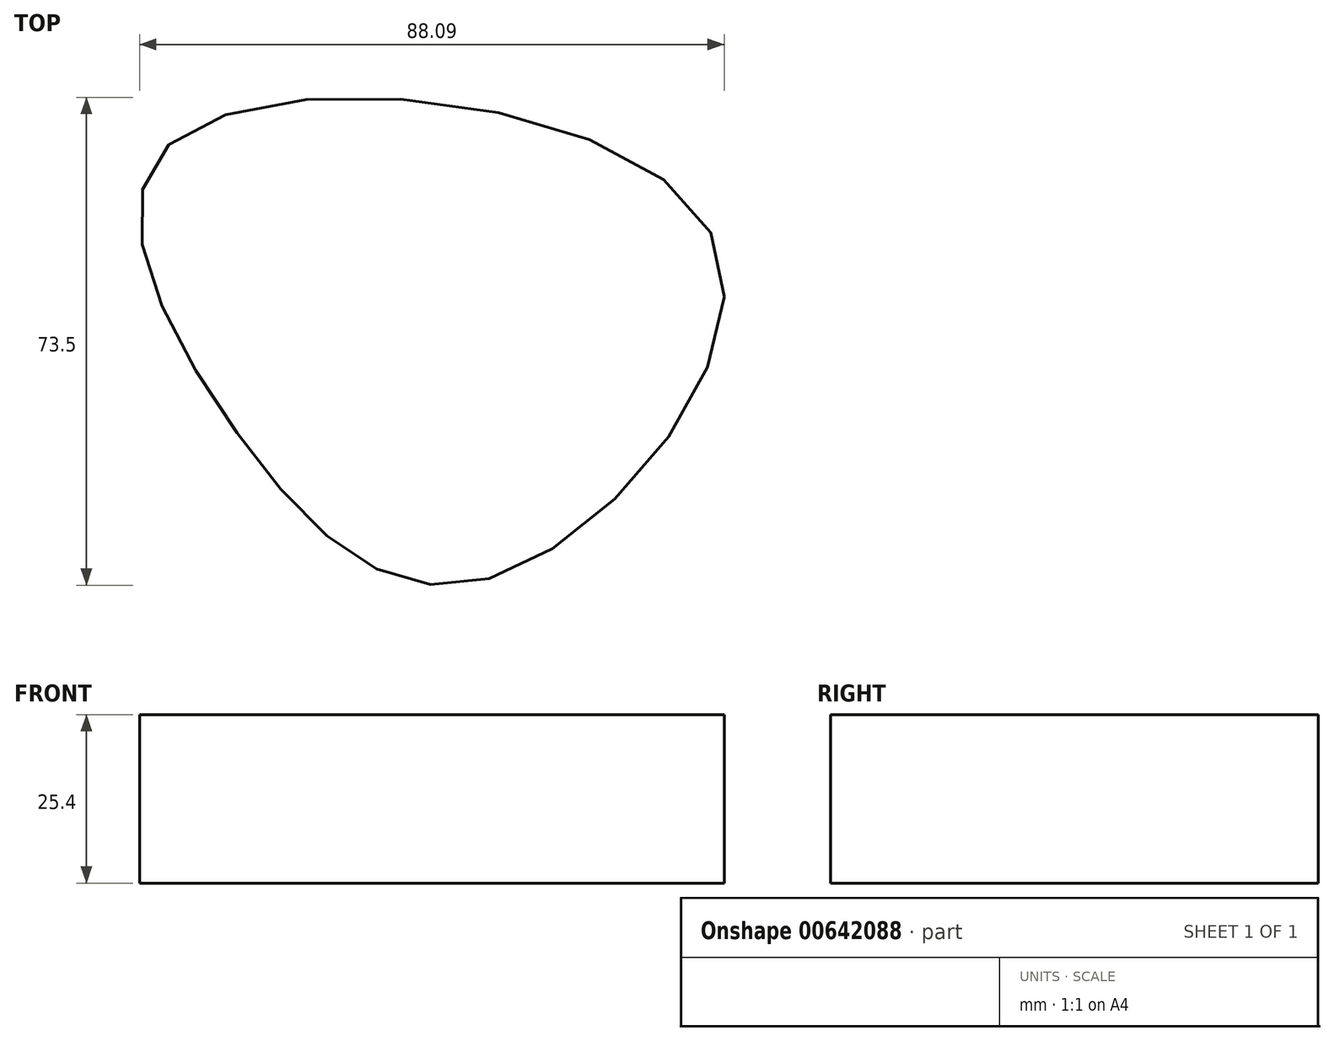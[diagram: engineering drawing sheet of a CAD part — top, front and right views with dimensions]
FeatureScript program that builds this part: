
annotation { "Feature Type Name" : "Feature", "Feature Type Description" : "" }
export const myFeature = defineFeature(function(context is Context, id is Id, definition is map)
    precondition{}
    {
        {
            var Q0;
            Q0=qCreatedBy(makeId("Top.planeOp"),FACE);
            var sketch = newSketch(context, id + "F0", { "sketchPlane" : qUnion([Q0])});
            skFitSpline(sketch, "E0", {"points": [v(-38.43, -12.93) * mm, v(-48.04, 31.04) * mm, v(32.89, 17.37) * mm, v(0, -34.74) * mm, v(-38.43, -12.93) * mm]});
            skSolve(sketch);
        }
        {
            var Q0;
            Q0 = qSketchRegion(id + "F0", true);
            extrude(context, id + "F1", {"entities" : qUnion([Q0]), "depth" : 25.4 * mm, "offsetDistance" : 25.4 * mm});
        }
    });
